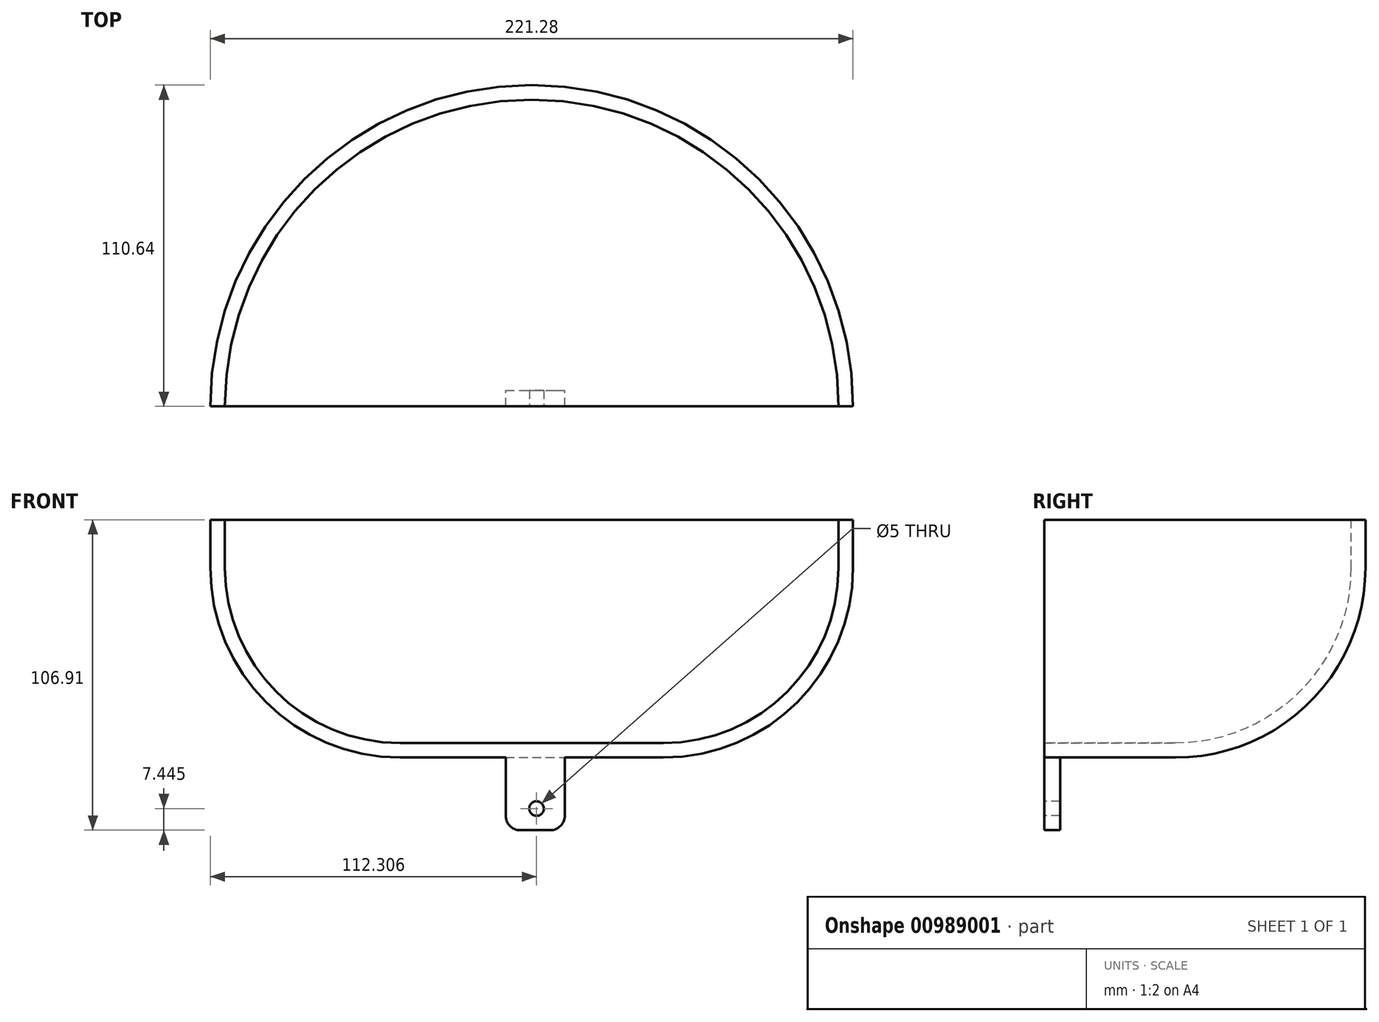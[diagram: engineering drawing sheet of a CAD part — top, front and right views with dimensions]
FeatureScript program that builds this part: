
annotation { "Feature Type Name" : "Feature", "Feature Type Description" : "" }
export const myFeature = defineFeature(function(context is Context, id is Id, definition is map)
    precondition{}
    {
        {
            var Q0;
            Q0=qCreatedBy(makeId("Front.planeOp"),FACE);
            var sketch = newSketch(context, id + "F0", { "sketchPlane" : qUnion([Q0])});
            skArc(sketch, "E0", {"start": v(0, -65.34) * mm, "mid": v(46.2, -46.2) * mm, "end": v(65.34, 0) * mm});
            skArc(sketch, "E1", {"start": v(0, -60.34) * mm, "mid": v(42.66, -42.66) * mm, "end": v(60.34, 0) * mm});
            skLineSegment(sketch, "E2.bottom", {"start": v(0, -65.34) * mm, "end": v(-45.3, -65.34) * mm});
            skLineSegment(sketch, "E2.top", {"start": v(0, -60.34) * mm, "end": v(-45.3, -60.34) * mm});
            skLineSegment(sketch, "E2.right", {"start": v(-45.3, -65.34) * mm, "end": v(-45.3, -60.34) * mm});
            skLineSegment(sketch, "E3.bottom", {"start": v(60.34, 0) * mm, "end": v(60.34, 0) * mm});
            skLineSegment(sketch, "E3.top", {"start": v(65.34, 16.57) * mm, "end": v(60.34, 16.57) * mm});
            skLineSegment(sketch, "E3.left", {"start": v(65.34, 0) * mm, "end": v(65.34, 16.57) * mm});
            skLineSegment(sketch, "E3.right", {"start": v(60.34, 0) * mm, "end": v(60.34, 16.57) * mm});
            skSolve(sketch);
        }
        {
            var Q0;
            Q0 = qSketchRegion(id + "F0", true);
            var Q1;
            Q1=sQuery(id+"F0.wireOp",EDGE,"E2.right");
            revolve(context, id + "F1", {"surfaceOperationType" : NewSurfaceOperationType.NEW, "entities" : qUnion([Q0]), "axis" : qUnion([Q1]), "revolveType" : RevolveType.ONE_DIRECTION, "angle" : 180 * degree});
        }
        {
            var Q0;
            Q0=makeQuery(id+"F1.opRevolve","SWEPT_FACE",FACE,{"disambiguationData":[OSD([sQuery(id+"F0.wireOp",EDGE,"E2.bottom")])]});
            var sketch = newSketch(context, id + "F2", { "sketchPlane" : qUnion([Q0])});
            skLineSegment(sketch, "E4.bottom", {"start": v(12808.88, 1005.5) * mm, "end": v(11605.46, 1005.5) * mm});
            skLineSegment(sketch, "E4.top", {"start": v(12808.88, 909.2) * mm, "end": v(11605.46, 909.2) * mm});
            skLineSegment(sketch, "E4.left", {"start": v(12808.88, 1005.5) * mm, "end": v(12808.88, 909.2) * mm});
            skLineSegment(sketch, "E4.right", {"start": v(11605.46, 1005.5) * mm, "end": v(11605.46, 909.2) * mm});
            skLineSegment(sketch, "E5.bottom", {"start": v(-54.25, 0) * mm, "end": v(-33.92, 0) * mm});
            skLineSegment(sketch, "E5.top", {"start": v(-54.25, -5.54) * mm, "end": v(-33.92, -5.54) * mm});
            skLineSegment(sketch, "E5.left", {"start": v(-54.25, 0) * mm, "end": v(-54.25, -5.54) * mm});
            skLineSegment(sketch, "E5.right", {"start": v(-33.92, 0) * mm, "end": v(-33.92, -5.54) * mm});
            skSolve(sketch);
        }
        {
            var Q0;
            Q0=makeQuery(id+"F2.imprint","IMPRINT",FACE,{"disambiguationData":[TD([[makeQuery(id+"F2.imprint","IMPRINT",EDGE,{"derivedFrom":sQuery(id+"F2.wireOp",EDGE,"E5.bottom")}),-1.0]])]});
            extrude(context, id + "F3", {"entities" : qUnion([Q0]), "operationType" : NewBodyOperationType.ADD, "depth" : 25 * mm, "offsetDistance" : 25 * mm});
        }
        {
            var Q0;
            Q0=makeQuery(id+"F3.opExtrude","CAP_EDGE",EDGE,{"disambiguationData":[OSD([sQuery(id+"F2.wireOp",EDGE,"E5.right")])],"isStart":false});
            var Q1;
            Q1=makeQuery(id+"F3.opExtrude","CAP_EDGE",EDGE,{"disambiguationData":[OSD([sQuery(id+"F2.wireOp",EDGE,"E5.left")])],"isStart":false});
            fillet(context, id + "F4", {"entities" : qUnion([Q0, Q1]), "radius" : 5 * mm, "tangentPropagation" : true, "allowEdgeOverflow" : false});
        }
        {
            var Q0;
            Q0=makeQuery(id+"F3.boolean.opBoolean","MERGE",FACE,{"derivedFrom":[makeQuery(id+"F1.opRevolve","CAP_FACE",FACE,{"disambiguationData":[OSD([sQuery(id+"F0.wireOp",EDGE,"E0"),sQuery(id+"F0.wireOp",EDGE,"E1"),sQuery(id+"F0.wireOp",EDGE,"E2.bottom"),sQuery(id+"F0.wireOp",EDGE,"E2.top"),sQuery(id+"F0.wireOp",EDGE,"E2.right"),sQuery(id+"F0.wireOp",EDGE,"E3.top"),sQuery(id+"F0.wireOp",EDGE,"E3.left"),sQuery(id+"F0.wireOp",EDGE,"E3.right")])],"isStart":false}),makeQuery(id+"F3.opExtrude","SWEPT_FACE",FACE,{"disambiguationData":[OSD([sQuery(id+"F2.wireOp",EDGE,"E5.bottom")])]})]});
            var sketch = newSketch(context, id + "F5", { "sketchPlane" : qUnion([Q0])});
            skPoint(sketch, "E6", {"position": v(-43.63, -82.9) * mm});
            skSolve(sketch);
        }
        {
            var Q0;
            Q0=sQuery(id+"F5.wireOp",VERTEX,"E6");
            var Q1;
            Q1=makeQuery(id+"F1.opRevolve","SWEPT_BODY",BODY,{"disambiguationData":[OSD([sQuery(id+"F0.wireOp",EDGE,"E0"),sQuery(id+"F0.wireOp",EDGE,"E1"),sQuery(id+"F0.wireOp",EDGE,"E2.bottom"),sQuery(id+"F0.wireOp",EDGE,"E2.top"),sQuery(id+"F0.wireOp",EDGE,"E2.right"),sQuery(id+"F0.wireOp",EDGE,"E3.top"),sQuery(id+"F0.wireOp",EDGE,"E3.left"),sQuery(id+"F0.wireOp",EDGE,"E3.right")])]});
            hole(context, id + "F6", {"style" : HoleStyle.SIMPLE, "endStyle" : HoleEndStyle.THROUGH, "holeDiameter" : 5 * mm, "majorDiameter" : 5 * mm, "isTappedThrough" : true, "tappedDepth" : 12 * mm, "tapClearance" : 3, "locations" : qUnion([Q0]), "scope" : qUnion([Q1])});
        }
    });
